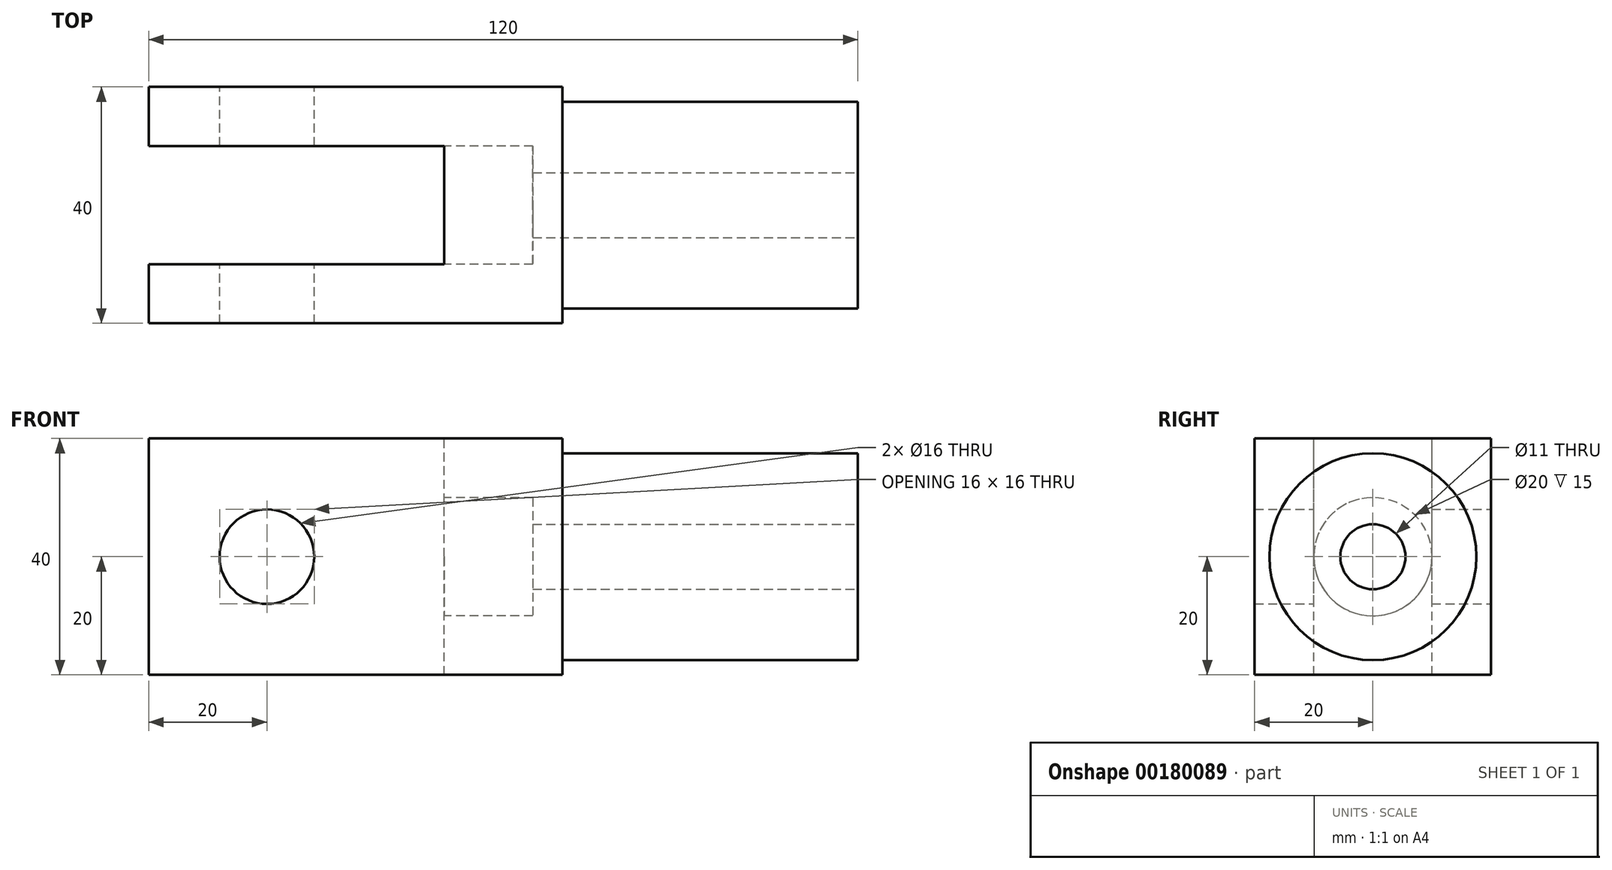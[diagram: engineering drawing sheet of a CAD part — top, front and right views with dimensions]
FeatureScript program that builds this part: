
annotation { "Feature Type Name" : "Feature", "Feature Type Description" : "" }
export const myFeature = defineFeature(function(context is Context, id is Id, definition is map)
    precondition{}
    {
        {
            var Q0;
            Q0=qCreatedBy(makeId("Right.planeOp"),FACE);
            var sketch = newSketch(context, id + "F0", { "sketchPlane" : qUnion([Q0])});
            skLineSegment(sketch, "E0.bottom", {"start": v(-20, -20) * mm, "end": v(20, -20) * mm});
            skLineSegment(sketch, "E0.top", {"start": v(-20, 20) * mm, "end": v(20, 20) * mm});
            skLineSegment(sketch, "E0.left", {"start": v(-20, -20) * mm, "end": v(-20, 20) * mm});
            skLineSegment(sketch, "E0.right", {"start": v(20, -20) * mm, "end": v(20, 20) * mm});
            skSolve(sketch);
        }
        {
            var Q0;
            Q0=makeQuery(id+"F0.imprint","IMPRINT",FACE,{"disambiguationData":[TD([[makeQuery(id+"F0.imprint","IMPRINT",EDGE,{"derivedFrom":sQuery(id+"F0.wireOp",EDGE,"E0.bottom")}),1.0]])]});
            extrude(context, id + "F1", {"entities" : qUnion([Q0]), "oppositeDirection" : true, "depth" : 120 * mm});
        }
        {
            var Q0;
            Q0=makeQuery(id+"F1.opExtrude","CAP_FACE",FACE,{"disambiguationData":[OSD([sQuery(id+"F0.wireOp",EDGE,"E0.bottom"),sQuery(id+"F0.wireOp",EDGE,"E0.top"),sQuery(id+"F0.wireOp",EDGE,"E0.left"),sQuery(id+"F0.wireOp",EDGE,"E0.right")])],"isStart":true});
            var sketch = newSketch(context, id + "F2", { "sketchPlane" : qUnion([Q0])});
            skCircle(sketch, "E1", {"center": v(0, 0) * mm, "radius": 17.5 * mm});
            skSolve(sketch);
        }
        {
            var Q0;
            Q0=makeQuery(id+"F2.imprint","IMPRINT",FACE,{"disambiguationData":[TD([[makeQuery(id+"F2.imprint","IMPRINT",EDGE,{"derivedFrom":sQuery(id+"F2.wireOp",EDGE,"E1")}),-1.0]])]});
            extrude(context, id + "F3", {"entities" : qUnion([Q0]), "operationType" : NewBodyOperationType.REMOVE, "oppositeDirection" : true, "depth" : 50 * mm});
        }
        {
            var Q0;
            Q0=makeQuery(id+"F1.opExtrude","CAP_FACE",FACE,{"disambiguationData":[OSD([sQuery(id+"F0.wireOp",EDGE,"E0.bottom"),sQuery(id+"F0.wireOp",EDGE,"E0.top"),sQuery(id+"F0.wireOp",EDGE,"E0.left"),sQuery(id+"F0.wireOp",EDGE,"E0.right")])],"isStart":true});
            var sketch = newSketch(context, id + "F4", { "sketchPlane" : qUnion([Q0])});
            skCircle(sketch, "E2", {"center": v(0, 0) * mm, "radius": 5.5 * mm});
            skSolve(sketch);
        }
        {
            var Q0;
            Q0=makeQuery(id+"F4.imprint","IMPRINT",FACE,{"disambiguationData":[TD([[makeQuery(id+"F4.imprint","IMPRINT",EDGE,{"derivedFrom":sQuery(id+"F4.wireOp",EDGE,"E2")}),1.0]])]});
            extrude(context, id + "F5", {"entities" : qUnion([Q0]), "operationType" : NewBodyOperationType.REMOVE, "oppositeDirection" : true, "depth" : 100 * mm});
        }
        {
            var Q0;
            Q0=makeQuery(id+"F1.opExtrude","CAP_FACE",FACE,{"disambiguationData":[OSD([sQuery(id+"F0.wireOp",EDGE,"E0.bottom"),sQuery(id+"F0.wireOp",EDGE,"E0.top"),sQuery(id+"F0.wireOp",EDGE,"E0.left"),sQuery(id+"F0.wireOp",EDGE,"E0.right")])],"isStart":false});
            var sketch = newSketch(context, id + "F6", { "sketchPlane" : qUnion([Q0])});
            skLineSegment(sketch, "E3.bottom", {"start": v(-10, -20) * mm, "end": v(10, -20) * mm});
            skLineSegment(sketch, "E3.top", {"start": v(-10, 20) * mm, "end": v(10, 20) * mm});
            skLineSegment(sketch, "E3.left", {"start": v(-10, -20) * mm, "end": v(-10, 20) * mm});
            skLineSegment(sketch, "E3.right", {"start": v(10, -20) * mm, "end": v(10, 20) * mm});
            skSolve(sketch);
        }
        {
            var Q0;
            Q0=makeQuery(id+"F6.imprint","IMPRINT",FACE,{"disambiguationData":[TD([[makeQuery(id+"F6.imprint","IMPRINT",EDGE,{"derivedFrom":sQuery(id+"F6.wireOp",EDGE,"E3.bottom")}),-1.0]])]});
            extrude(context, id + "F7", {"entities" : qUnion([Q0]), "operationType" : NewBodyOperationType.REMOVE, "oppositeDirection" : true, "depth" : 50 * mm});
        }
        {
            var Q0;
            Q0=makeQuery(id+"F7.boolean.opBoolean","COPY",FACE,{"derivedFrom":makeQuery(id+"F7.opExtrude","CAP_FACE",FACE,{"disambiguationData":[OSD([sQuery(id+"F6.wireOp",EDGE,"E3.bottom"),sQuery(id+"F6.wireOp",EDGE,"E3.top"),sQuery(id+"F6.wireOp",EDGE,"E3.left"),sQuery(id+"F6.wireOp",EDGE,"E3.right")])],"isStart":false})});
            var sketch = newSketch(context, id + "F8", { "sketchPlane" : qUnion([Q0])});
            skCircle(sketch, "E4", {"center": v(0, 0) * mm, "radius": 10 * mm});
            skSolve(sketch);
        }
        {
            var Q0;
            Q0 = qSketchRegion(id + "F8", true);
            extrude(context, id + "F9", {"entities" : qUnion([Q0]), "operationType" : NewBodyOperationType.REMOVE, "oppositeDirection" : true, "depth" : 15 * mm});
        }
        {
            var Q0;
            Q0=makeQuery(id+"F1.opExtrude","SWEPT_FACE",FACE,{"disambiguationData":[OSD([sQuery(id+"F0.wireOp",EDGE,"E0.left")])]});
            var sketch = newSketch(context, id + "F10", { "sketchPlane" : qUnion([Q0])});
            skCircle(sketch, "E5", {"center": v(-100, 0) * mm, "radius": 8 * mm});
            skSolve(sketch);
        }
        {
            var Q0;
            Q0 = qSketchRegion(id + "F10", true);
            extrude(context, id + "F11", {"entities" : qUnion([Q0]), "operationType" : NewBodyOperationType.REMOVE, "endBound" : BoundingType.SYMMETRIC, "depth" : 120 * mm});
        }
    });
